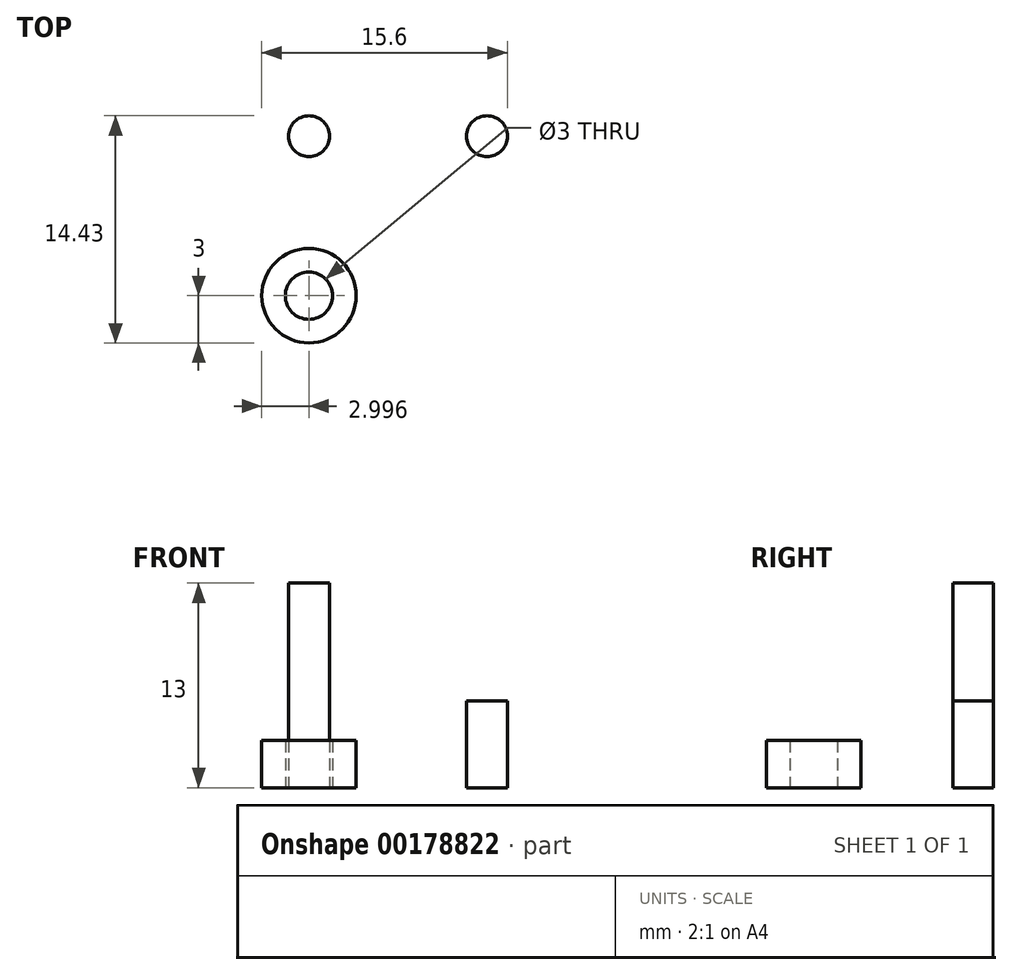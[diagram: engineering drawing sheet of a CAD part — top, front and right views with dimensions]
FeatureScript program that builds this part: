
annotation { "Feature Type Name" : "Feature", "Feature Type Description" : "" }
export const myFeature = defineFeature(function(context is Context, id is Id, definition is map)
    precondition{}
    {
        {
            var Q0;
            Q0=qCreatedBy(makeId("Top.planeOp"),FACE);
            var sketch = newSketch(context, id + "F0", { "sketchPlane" : qUnion([Q0])});
            skCircle(sketch, "E0", {"center": v(-5.83, 3.1) * mm, "radius": 1.3 * mm});
            skCircle(sketch, "E1", {"center": v(-5.83, -7.03) * mm, "radius": 3 * mm});
            skCircle(sketch, "E2", {"center": v(-5.83, -7.03) * mm, "radius": 1.5 * mm});
            skCircle(sketch, "E3.0.1.0", {"center": v(5.47, 3.1) * mm, "radius": 1.3 * mm});
            skSolve(sketch);
        }
        {
            var Q0;
            Q0=makeQuery(id+"F0.imprint","IMPRINT",FACE,{"disambiguationData":[TD([[makeQuery(id+"F0.imprint","IMPRINT",EDGE,{"derivedFrom":sQuery(id+"F0.wireOp",EDGE,"E3.0.1.0")}),1.0]])]});
            extrude(context, id + "F1", {"entities" : qUnion([Q0]), "depth" : 5.5 * mm});
        }
        {
            var Q0;
            Q0=makeQuery(id+"F0.imprint","IMPRINT",FACE,{"disambiguationData":[TD([[makeQuery(id+"F0.imprint","IMPRINT",EDGE,{"derivedFrom":sQuery(id+"F0.wireOp",EDGE,"E0")}),1.0]])]});
            extrude(context, id + "F2", {"entities" : qUnion([Q0]), "depth" : 13 * mm});
        }
        {
            var Q0;
            Q0=makeQuery(id+"F0.imprint","IMPRINT",FACE,{"disambiguationData":[TD([[makeQuery(id+"F0.imprint","IMPRINT",EDGE,{"derivedFrom":sQuery(id+"F0.wireOp",EDGE,"E1")}),1.0]])]});
            extrude(context, id + "F3", {"entities" : qUnion([Q0]), "depth" : 3 * mm});
        }
    });
